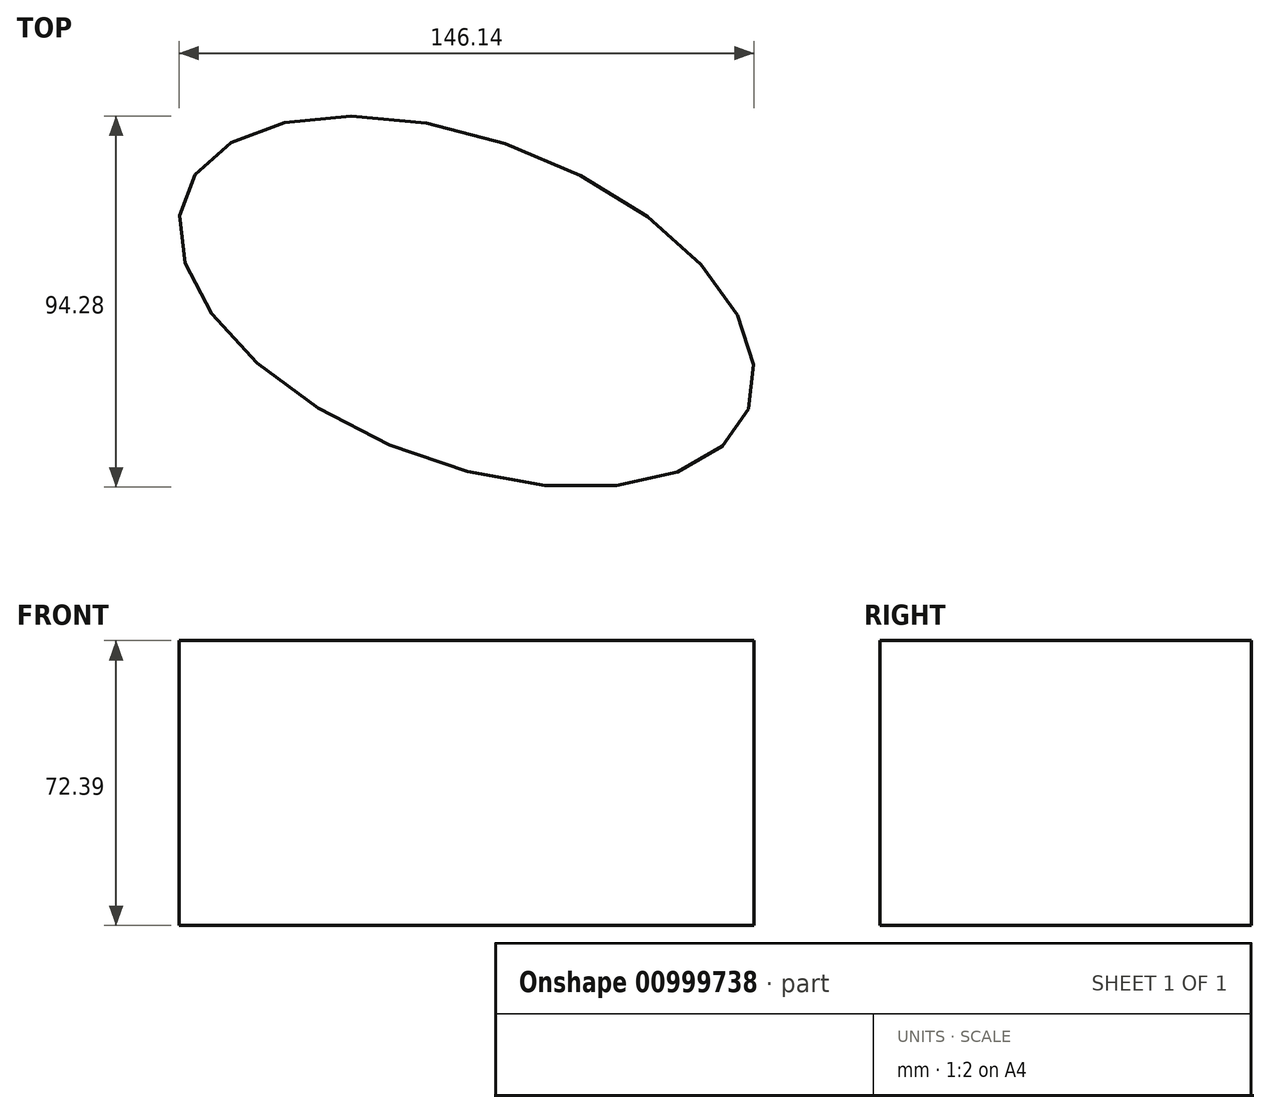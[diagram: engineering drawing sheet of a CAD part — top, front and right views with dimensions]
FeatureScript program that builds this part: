
annotation { "Feature Type Name" : "Feature", "Feature Type Description" : "" }
export const myFeature = defineFeature(function(context is Context, id is Id, definition is map)
    precondition{}
    {
        {
            var Q0;
            Q0=qCreatedBy(makeId("Top.planeOp"),FACE);
            var sketch = newSketch(context, id + "F0", { "sketchPlane" : qUnion([Q0])});
            skEllipse(sketch, "E0", {"center": v(0, 0) * mm, "majorRadius": 76.62 * mm, "minorRadius": 41.11 * mm, "majorAxis": v(0.93, -0.36)});
            skSolve(sketch);
        }
        {
            var Q0;
            Q0 = qSketchRegion(id + "F0", true);
            extrude(context, id + "F1", {"entities" : qUnion([Q0]), "depth" : 25.4 * mm, "offsetDistance" : 25.4 * mm});
        }
        {
            var Q0;
            Q0=makeQuery(id+"F1.opExtrude","CAP_FACE",FACE,{"disambiguationData":[OSD([sQuery(id+"F0.wireOp",EDGE,"E0")])],"isStart":false});
            extrude(context, id + "F2", {"entities" : qUnion([Q0]), "operationType" : NewBodyOperationType.ADD, "depth" : 47 * mm, "offsetDistance" : 25.4 * mm});
        }
        {
            var Q0;
            Q0=makeQuery(id+"F1.opExtrude","CAP_FACE",FACE,{"disambiguationData":[OSD([sQuery(id+"F0.wireOp",EDGE,"E0")])],"isStart":true});
            extrude(context, id + "F3", {"entities" : qUnion([Q0]), "operationType" : NewBodyOperationType.ADD, "oppositeDirection" : true, "depth" : 51.82 * mm, "offsetDistance" : 25.4 * mm});
        }
        {
            var Q0;
            Q0=makeQuery(id+"F1.opExtrude","CAP_FACE",FACE,{"disambiguationData":[OSD([sQuery(id+"F0.wireOp",EDGE,"E0")])],"isStart":true});
            extrude(context, id + "F4", {"entities" : qUnion([Q0]), "operationType" : NewBodyOperationType.ADD, "oppositeDirection" : true, "depth" : 65.28 * mm, "offsetDistance" : 25.4 * mm});
        }
    });
